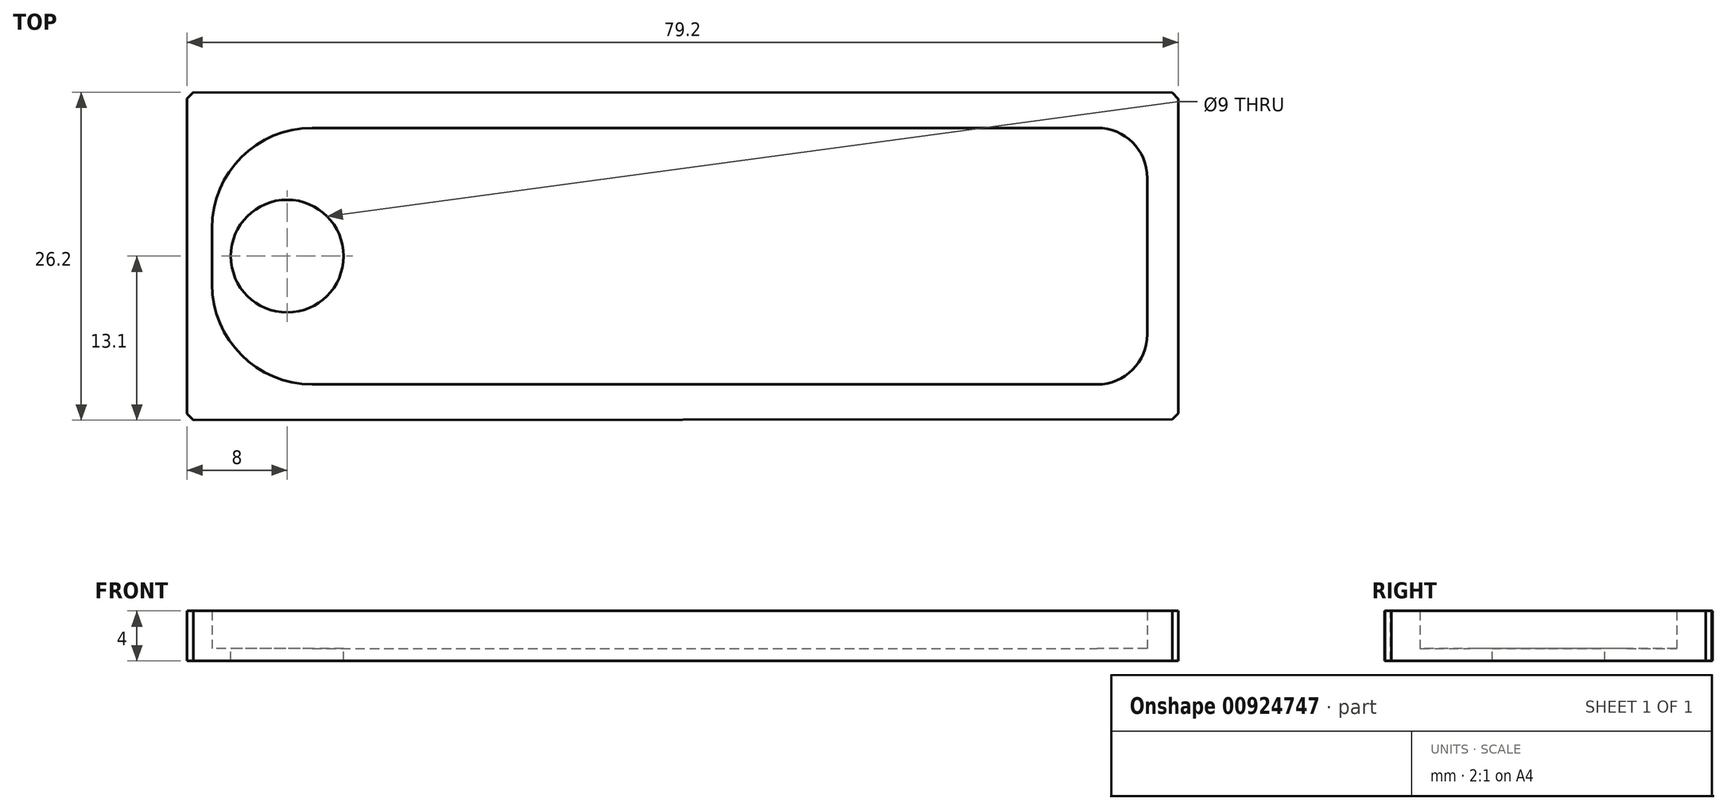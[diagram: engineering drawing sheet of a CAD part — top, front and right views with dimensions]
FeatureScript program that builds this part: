
annotation { "Feature Type Name" : "Feature", "Feature Type Description" : "" }
export const myFeature = defineFeature(function(context is Context, id is Id, definition is map)
    precondition{}
    {
        {
            var Q0;
            Q0=qCreatedBy(makeId("Top.planeOp"),FACE);
            var sketch = newSketch(context, id + "F0", { "sketchPlane" : qUnion([Q0])});
            skLineSegment(sketch, "E0.bottom", {"start": v(2, 10.25) * mm, "end": v(64.7, 10.25) * mm});
            skLineSegment(sketch, "E0.top", {"start": v(2, -10.25) * mm, "end": v(64.7, -10.25) * mm});
            skLineSegment(sketch, "E0.left", {"start": v(-6, 2.25) * mm, "end": v(-6, -2.25) * mm});
            skLineSegment(sketch, "E0.right", {"start": v(68.7, 6.25) * mm, "end": v(68.7, -6.25) * mm});
            skLineSegment(sketch, "E1", {"start": v(-6, 0) * mm, "end": v(0, 0) * mm, "construction": true});
            skCircle(sketch, "E2", {"center": v(0, 0) * mm, "radius": 4.5 * mm});
            skLineSegment(sketch, "E3.bottom", {"start": v(-8, 13.1) * mm, "end": v(71.2, 13.05) * mm});
            skLineSegment(sketch, "E3.top", {"start": v(-8, -13.1) * mm, "end": v(71.2, -13.05) * mm});
            skLineSegment(sketch, "E3.left", {"start": v(-8, 13.1) * mm, "end": v(-8, -13.1) * mm});
            skLineSegment(sketch, "E3.right", {"start": v(71.2, 13.05) * mm, "end": v(71.2, -13.05) * mm});
            skLineSegment(sketch, "E4", {"start": v(-6, 0) * mm, "end": v(-8, 0) * mm, "construction": true});
            skLineSegment(sketch, "E5", {"start": v(68.7, 0) * mm, "end": v(71.2, 0) * mm, "construction": true});
            skPoint(sketch, "E6.visualSharp", {"position": v(-6, 10.25) * mm});
            skArc(sketch, "E6.filletArc", {"start": v(2, 10.25) * mm, "mid": v(-3.66, 7.9) * mm, "end": v(-6, 2.25) * mm});
            skPoint(sketch, "E7.visualSharp", {"position": v(-6, -10.25) * mm});
            skArc(sketch, "E7.filletArc", {"start": v(-6, -2.25) * mm, "mid": v(-3.66, -7.9) * mm, "end": v(2, -10.25) * mm});
            skPoint(sketch, "E8.visualSharp", {"position": v(68.7, 10.25) * mm});
            skArc(sketch, "E8.filletArc", {"start": v(68.7, 6.25) * mm, "mid": v(67.53, 9.08) * mm, "end": v(64.7, 10.25) * mm});
            skPoint(sketch, "E9.visualSharp", {"position": v(68.7, -10.25) * mm});
            skArc(sketch, "E9.filletArc", {"start": v(64.7, -10.25) * mm, "mid": v(67.53, -9.08) * mm, "end": v(68.7, -6.25) * mm});
            skSolve(sketch);
        }
        {
            var Q0;
            Q0=makeQuery(id+"F0.imprint","IMPRINT",FACE,{"disambiguationData":[TD([[makeQuery(id+"F0.imprint","IMPRINT",EDGE,{"derivedFrom":sQuery(id+"F0.wireOp",EDGE,"E0.bottom")}),1.0]])]});
            extrude(context, id + "F1", {"entities" : qUnion([Q0]), "depth" : 3 * mm, "offsetDistance" : 25 * mm});
        }
        {
            var Q0;
            Q0=makeQuery(id+"F0.imprint","IMPRINT",FACE,{"disambiguationData":[TD([[makeQuery(id+"F0.imprint","IMPRINT",EDGE,{"derivedFrom":sQuery(id+"F0.wireOp",EDGE,"E0.bottom")}),-1.0]])]});
            var Q1;
            Q1=makeQuery(id+"F0.imprint","IMPRINT",FACE,{"disambiguationData":[TD([[makeQuery(id+"F0.imprint","IMPRINT",EDGE,{"derivedFrom":sQuery(id+"F0.wireOp",EDGE,"E0.bottom")}),1.0]])]});
            extrude(context, id + "F2", {"entities" : qUnion([Q0, Q1]), "operationType" : NewBodyOperationType.ADD, "oppositeDirection" : true, "depth" : 1 * mm, "offsetDistance" : 25 * mm});
        }
        {
            var Q0;
            {var subQ0=sQuery(id+"F0.wireOp",EDGE,"E3.left");var subQ1=sQuery(id+"F0.wireOp",EDGE,"E3.top");Q0=makeQuery(id+"F2.boolean.opBoolean","MERGE",EDGE,{"derivedFrom":[makeQuery(id+"F1.opExtrude","SWEPT_EDGE",EDGE,{"disambiguationData":[OSD([subQ1,subQ0])]}),makeQuery(id+"F2.opExtrude","SWEPT_EDGE",EDGE,{"disambiguationData":[OSD([subQ1,subQ0])]})]});}
            var Q1;
            {var subQ0=sQuery(id+"F0.wireOp",EDGE,"E3.left");var subQ1=sQuery(id+"F0.wireOp",EDGE,"E3.bottom");Q1=makeQuery(id+"F2.boolean.opBoolean","MERGE",EDGE,{"derivedFrom":[makeQuery(id+"F1.opExtrude","SWEPT_EDGE",EDGE,{"disambiguationData":[OSD([subQ1,subQ0])]}),makeQuery(id+"F2.opExtrude","SWEPT_EDGE",EDGE,{"disambiguationData":[OSD([subQ1,subQ0])]})]});}
            var Q2;
            {var subQ0=sQuery(id+"F0.wireOp",EDGE,"E3.right");var subQ1=sQuery(id+"F0.wireOp",EDGE,"E3.top");Q2=makeQuery(id+"F2.boolean.opBoolean","MERGE",EDGE,{"derivedFrom":[makeQuery(id+"F1.opExtrude","SWEPT_EDGE",EDGE,{"disambiguationData":[OSD([subQ1,subQ0])]}),makeQuery(id+"F2.opExtrude","SWEPT_EDGE",EDGE,{"disambiguationData":[OSD([subQ1,subQ0])]})]});}
            var Q3;
            {var subQ0=sQuery(id+"F0.wireOp",EDGE,"E3.right");var subQ1=sQuery(id+"F0.wireOp",EDGE,"E3.bottom");Q3=makeQuery(id+"F2.boolean.opBoolean","MERGE",EDGE,{"derivedFrom":[makeQuery(id+"F1.opExtrude","SWEPT_EDGE",EDGE,{"disambiguationData":[OSD([subQ1,subQ0])]}),makeQuery(id+"F2.opExtrude","SWEPT_EDGE",EDGE,{"disambiguationData":[OSD([subQ1,subQ0])]})]});}
            chamfer(context, id + "F3", {"entities" : qUnion([Q0, Q1, Q2, Q3]), "width" : 0.5 * mm, "tangentPropagation" : true});
        }
    });
